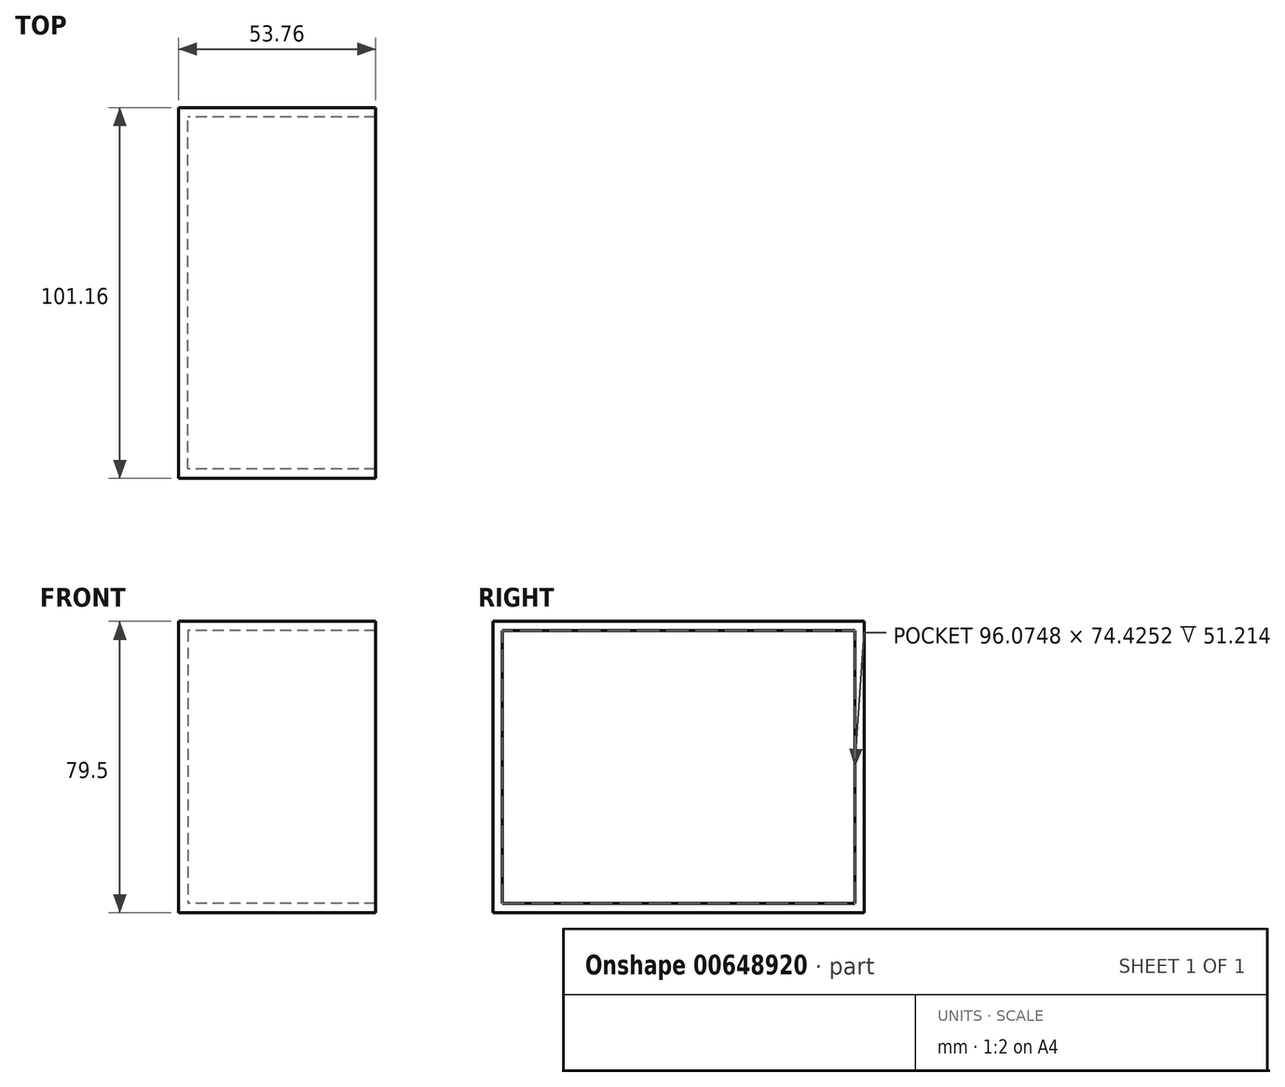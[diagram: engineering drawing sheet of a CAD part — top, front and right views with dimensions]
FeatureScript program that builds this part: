
annotation { "Feature Type Name" : "Feature", "Feature Type Description" : "" }
export const myFeature = defineFeature(function(context is Context, id is Id, definition is map)
    precondition{}
    {
        {
            var Q0;
            Q0=qCreatedBy(makeId("Right.planeOp"),FACE);
            var sketch = newSketch(context, id + "F0", { "sketchPlane" : qUnion([Q0])});
            skLineSegment(sketch, "E0.bottom", {"start": v(-48.06, 38.07) * mm, "end": v(53.1, 38.07) * mm});
            skLineSegment(sketch, "E0.top", {"start": v(-48.06, -41.43) * mm, "end": v(53.1, -41.43) * mm});
            skLineSegment(sketch, "E0.left", {"start": v(-48.06, 38.07) * mm, "end": v(-48.06, -41.43) * mm});
            skLineSegment(sketch, "E0.right", {"start": v(53.1, 38.07) * mm, "end": v(53.1, -41.43) * mm});
            skSolve(sketch);
        }
        {
            var Q0;
            Q0=makeQuery(id+"F0.imprint","IMPRINT",FACE,{"disambiguationData":[TD([[makeQuery(id+"F0.imprint","IMPRINT",EDGE,{"derivedFrom":sQuery(id+"F0.wireOp",EDGE,"E0.bottom")}),-1.0]])]});
            extrude(context, id + "F1", {"entities" : qUnion([Q0]), "endBound" : BoundingType.SYMMETRIC, "depth" : 53.75 * mm, "offsetDistance" : 25.4 * mm});
        }
        {
            var Q0;
            Q0=makeQuery(id+"F1.opExtrude","CAP_FACE",FACE,{"disambiguationData":[OSD([sQuery(id+"F0.wireOp",EDGE,"E0.bottom"),sQuery(id+"F0.wireOp",EDGE,"E0.top"),sQuery(id+"F0.wireOp",EDGE,"E0.left"),sQuery(id+"F0.wireOp",EDGE,"E0.right")])],"isStart":false});
            shell(context, id + "F2", {"entities" : qUnion([Q0]), "thickness" : 2.54 * mm});
        }
    });
